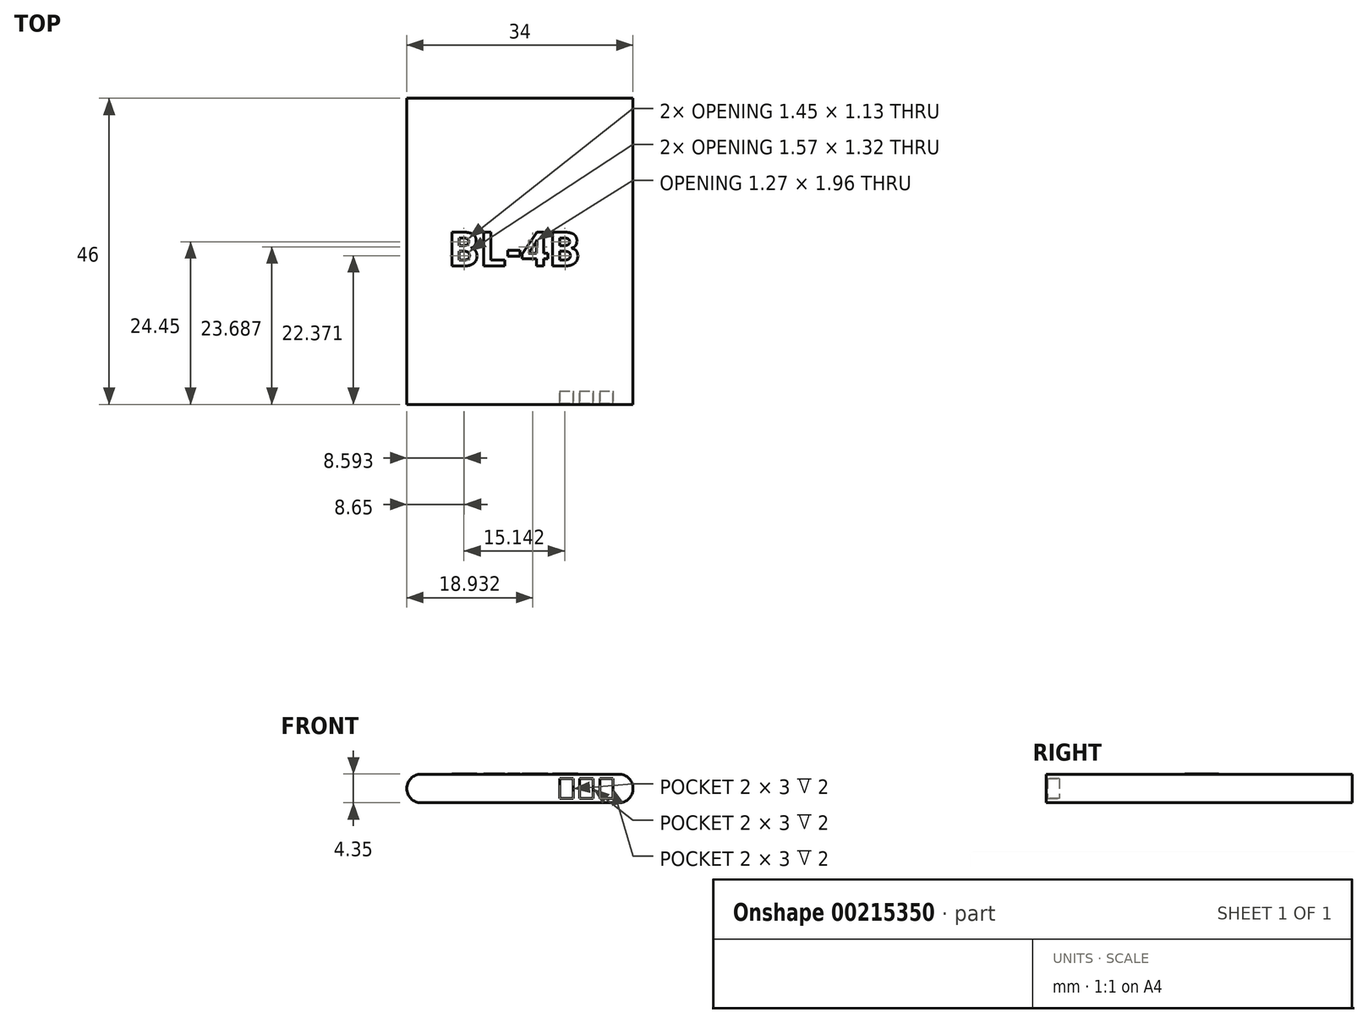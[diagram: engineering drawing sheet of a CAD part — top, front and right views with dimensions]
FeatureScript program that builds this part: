
annotation { "Feature Type Name" : "Feature", "Feature Type Description" : "" }
export const myFeature = defineFeature(function(context is Context, id is Id, definition is map)
    precondition{}
    {
        {
            var Q0;
            Q0=qCreatedBy(makeId("Top.planeOp"),FACE);
            var sketch = newSketch(context, id + "F0", { "sketchPlane" : qUnion([Q0])});
            skLineSegment(sketch, "E0.bottom", {"start": v(-17, 23) * mm, "end": v(17, 23) * mm});
            skLineSegment(sketch, "E0.top", {"start": v(-17, -23) * mm, "end": v(17, -23) * mm});
            skLineSegment(sketch, "E0.left", {"start": v(-17, 23) * mm, "end": v(-17, -23) * mm});
            skLineSegment(sketch, "E0.right", {"start": v(17, 23) * mm, "end": v(17, -23) * mm});
            skPoint(sketch, "E0.middle", {"position": v(0, 0) * mm});
            skSolve(sketch);
        }
        {
            var Q0;
            Q0 = qSketchRegion(id + "F0", true);
            extrude(context, id + "F1", {"entities" : qUnion([Q0]), "depth" : 4.3 * mm});
        }
        {
            var Q0;
            Q0=makeQuery(id+"F1.opExtrude","CAP_EDGE",EDGE,{"disambiguationData":[OSD([sQuery(id+"F0.wireOp",EDGE,"E0.left")])],"isStart":false});
            var Q1;
            Q1=makeQuery(id+"F1.opExtrude","CAP_EDGE",EDGE,{"disambiguationData":[OSD([sQuery(id+"F0.wireOp",EDGE,"E0.right")])],"isStart":false});
            var Q2;
            Q2=makeQuery(id+"F1.opExtrude","CAP_EDGE",EDGE,{"disambiguationData":[OSD([sQuery(id+"F0.wireOp",EDGE,"E0.right")])],"isStart":true});
            var Q3;
            Q3=makeQuery(id+"F1.opExtrude","CAP_EDGE",EDGE,{"disambiguationData":[OSD([sQuery(id+"F0.wireOp",EDGE,"E0.left")])],"isStart":true});
            fillet(context, id + "F2", {"entities" : qUnion([Q0, Q1, Q2, Q3]), "radius" : 2.15 * mm, "tangentPropagation" : true, "allowEdgeOverflow" : false});
        }
        {
            var Q0;
            Q0=makeQuery(id+"F1.opExtrude","SWEPT_FACE",FACE,{"disambiguationData":[OSD([sQuery(id+"F0.wireOp",EDGE,"E0.top")])]});
            var sketch = newSketch(context, id + "F3", { "sketchPlane" : qUnion([Q0])});
            skLineSegment(sketch, "E1.bottom", {"start": v(12, 3.65) * mm, "end": v(14, 3.65) * mm});
            skLineSegment(sketch, "E1.top", {"start": v(12, 0.65) * mm, "end": v(14, 0.65) * mm});
            skLineSegment(sketch, "E1.left", {"start": v(12, 3.65) * mm, "end": v(12, 0.65) * mm});
            skLineSegment(sketch, "E1.right", {"start": v(14, 3.65) * mm, "end": v(14, 0.65) * mm});
            skPoint(sketch, "E1.middle", {"position": v(13, 2.15) * mm});
            skPoint(sketch, "E2.1.0.0", {"position": v(10, 2.15) * mm});
            skLineSegment(sketch, "E2.1.0.1", {"start": v(11, 3.65) * mm, "end": v(11, 0.65) * mm});
            skLineSegment(sketch, "E2.1.0.2", {"start": v(9, 3.65) * mm, "end": v(9, 0.65) * mm});
            skLineSegment(sketch, "E2.1.0.3", {"start": v(9, 0.65) * mm, "end": v(11, 0.65) * mm});
            skLineSegment(sketch, "E2.1.0.4", {"start": v(9, 3.65) * mm, "end": v(11, 3.65) * mm});
            skPoint(sketch, "E2.2.0.0", {"position": v(7, 2.15) * mm});
            skLineSegment(sketch, "E2.2.0.1", {"start": v(8, 3.65) * mm, "end": v(8, 0.65) * mm});
            skLineSegment(sketch, "E2.2.0.2", {"start": v(6, 3.65) * mm, "end": v(6, 0.65) * mm});
            skLineSegment(sketch, "E2.2.0.3", {"start": v(6, 0.65) * mm, "end": v(8, 0.65) * mm});
            skLineSegment(sketch, "E2.2.0.4", {"start": v(6, 3.65) * mm, "end": v(8, 3.65) * mm});
            skLineSegment(sketch, "E2.direction1", {"start": v(12, 0.65) * mm, "end": v(9, 0.65) * mm, "construction": true});
            skSolve(sketch);
        }
        {
            var Q0;
            Q0 = qSketchRegion(id + "F3", true);
            extrude(context, id + "F4", {"entities" : qUnion([Q0]), "operationType" : NewBodyOperationType.REMOVE, "oppositeDirection" : true, "depth" : 2 * mm});
        }
        {
            var Q0;
            Q0=makeQuery(id+"F4.boolean.opBoolean","COPY",FACE,{"derivedFrom":makeQuery(id+"F4.opExtrude","CAP_FACE",FACE,{"disambiguationData":[OSD([sQuery(id+"F3.wireOp",EDGE,"E2.2.0.1"),sQuery(id+"F3.wireOp",EDGE,"E2.2.0.2"),sQuery(id+"F3.wireOp",EDGE,"E2.2.0.3"),sQuery(id+"F3.wireOp",EDGE,"E2.2.0.4")])],"isStart":false})});
            var sketch = newSketch(context, id + "F5", { "sketchPlane" : qUnion([Q0])});
            skLineSegment(sketch, "E3.bottom", {"start": v(6, 3.65) * mm, "end": v(8, 3.65) * mm});
            skLineSegment(sketch, "E3.top", {"start": v(6, 0.65) * mm, "end": v(8, 0.65) * mm});
            skLineSegment(sketch, "E3.left", {"start": v(6, 3.65) * mm, "end": v(6, 0.65) * mm});
            skLineSegment(sketch, "E3.right", {"start": v(8, 3.65) * mm, "end": v(8, 0.65) * mm});
            skLineSegment(sketch, "E4.1.0.0", {"start": v(9, 0.65) * mm, "end": v(11, 0.65) * mm});
            skLineSegment(sketch, "E4.1.0.1", {"start": v(9, 3.65) * mm, "end": v(9, 0.65) * mm});
            skLineSegment(sketch, "E4.1.0.2", {"start": v(11, 3.65) * mm, "end": v(11, 0.65) * mm});
            skLineSegment(sketch, "E4.1.0.3", {"start": v(9, 3.65) * mm, "end": v(11, 3.65) * mm});
            skLineSegment(sketch, "E4.2.0.0", {"start": v(12, 0.65) * mm, "end": v(14, 0.65) * mm});
            skLineSegment(sketch, "E4.2.0.1", {"start": v(12, 3.65) * mm, "end": v(12, 0.65) * mm});
            skLineSegment(sketch, "E4.2.0.2", {"start": v(14, 3.65) * mm, "end": v(14, 0.65) * mm});
            skLineSegment(sketch, "E4.2.0.3", {"start": v(12, 3.65) * mm, "end": v(14, 3.65) * mm});
            skLineSegment(sketch, "E4.direction1", {"start": v(6, 0.65) * mm, "end": v(9, 0.65) * mm, "construction": true});
            skSolve(sketch);
        }
        {
            var Q0;
            Q0 = qSketchRegion(id + "F5", true);
            extrude(context, id + "F6", {"entities" : qUnion([Q0]), "depth" : 1.8 * mm});
        }
        {
            var Q0;
            Q0=makeQuery(id+"F1.opExtrude","CAP_FACE",FACE,{"disambiguationData":[OSD([sQuery(id+"F0.wireOp",EDGE,"E0.bottom"),sQuery(id+"F0.wireOp",EDGE,"E0.top"),sQuery(id+"F0.wireOp",EDGE,"E0.left"),sQuery(id+"F0.wireOp",EDGE,"E0.right")])],"isStart":false});
            var sketch = newSketch(context, id + "F7", { "sketchPlane" : qUnion([Q0])});
            skText(sketch, "E5", { "text": "BL-4B", "fontName": "OpenSans-Bold.ttf"});
            const initialGuessF7  = {"E5": [-0.01085, -0.00218, 1, 0, 0.00512]};
            skSetInitialGuess(sketch, initialGuessF7);
            skSolve(sketch);
        }
        {
            var Q0;
            Q0 = qSketchRegion(id + "F7", true);
            extrude(context, id + "F8", {"entities" : qUnion([Q0]), "depth" : 0.05 * mm});
        }
    });
